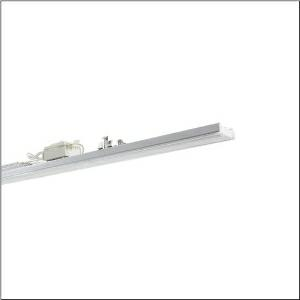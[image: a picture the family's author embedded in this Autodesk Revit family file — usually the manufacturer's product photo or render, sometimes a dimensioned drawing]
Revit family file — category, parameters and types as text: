
# Revit family: licross_11_recessed_mo_51te18dn695gd
name_source: partatom
category: Lighting Fixtures
units: mm (PartAtom-declared; Revit-internal decimal feet)

## family parameters
Cut with Voids When Loaded = No
Host = Face
Light Source = No
Part Type = Normal
Room Calculation Point = No
Round Connector Dimension = Use Diameter
Shared = No

## types (1)
- --- (1 x LED, 1450 lm, 9.2 W, 6500K)
    Apparent Load = 9 VA
    CIE Flux Codes = 83 96 99 100 100
    Color Rendering = 80
    Color Temperature = 6500K
    Default Elevation = 1800 mm
    Description = Licross 11 Recessed MO, luminaire insert, of sheet steel, galvanised, coil coated, white, length: 1.500mm, width: 66mm, height: 67mm, LED rated luminous flux: 9.710lm, light colour: 865, SDCM (Standard Deviation of Colour Matching)MacAdam ≤ 2 SDCM (initial), control gear: DALI 2 (for two DALI lines), with plug, 6-pole, with phase selection, mains connection: 220..240V, AC/DC, 0/50..60Hz, rated input power: 57W, internal wiring halogen-free, for central battery installations according to EN 60598-2-22, for emergency light function, without changeover relay, primary light control with lens, of plastic, primary optical cover: cover, of PMMA, light emission: direct distribution, primary light characteristic: symmetric, protection rating (complete): IP54, insulation class (complete): insulation class I (protective earthing), certification: CE, ENEC, VDE, UKCA, protection symbol: D if used in an environment with non-conductive dust loads with corresponding accessories, impact resistance: IK06, permissible ambient temperature for indoor applications: -25..+35°C, standard: EN 60598-2-22, corresponds to IFS (International Featured Standards) requirements for safety and quality in the food industry, reducing of maximum allowable ambient temperature of 5°C with ceiling mounting, LABS conformity tested according to VDMA 24364:2018-05, The light source and the operating device comply with the requirements of the Ecodesign Regulation (EU) 2019/2020 and are replaceable in accordance with this regulation, packaging unit: 1 piece
    Height = 58 mm
    Lamp = 1 x LED
    Lamp Light Flux = 1450 lm
    Lamp Power = 9.2 W
    Lamp count = 1
    Length = 1500 mm
    Luminous efficacy = 158 lm/W
    Manufacturer = Siteco
    ModVariant = No
    Model = 51TE18DN695GD
    Mounting Place = Ceiling
    Mounting Type = Pendant
    Number of Poles = 1
    OnlyDefault = Yes
    Power Factor = 1
    Product Name = Licross 11 Recessed MO
    Product group = luminaire insert | ceiling pendant
    ProductGroupID = 901
    Protection Class = Protection class I
    Protection Degree = IP 54
    RLX_Detail_Level = 1
    RLX_Emergency_Light_Flux = 0 lm
    RLX_Emergency_Type = 0
    RLX_Emergency_Type_DB = No
    RlxData = <blob elided: 25193 chars, md5=268e8f97>
    Socket = socket
    Standby Power = 0 W
    System Light Flux = 1450 lm
    System Power = 9 W
    Type Comments = : DC mode (central or group accumulator) initial emergency light level
    Type Image = l_1296930.jpg
    URL = http://relux.com
    VarID = @adj_030201
    Voltage = 0 V
    Weight = 0.00 kg
    Width = 66 mm

## geometry (parser evidence)
native form markers: Blend x4, Sweep x12
no freeform markers — native parametric forms only
